# Revit family: DC_Holyoake_OutsideLouver_OHCL-C-124_supply_12
name_source: partatom
category: Air Terminals
revit_build: Autodesk Revit 2013 (Build: 20120221_2030(x64)
units: mm (PartAtom-declared; Revit-internal decimal feet)

## types (2) — shared parameters
Accessories = Aluminium Bird mesh or insect mesh (fibreglass)
Blade Height = 89.8 mm
Blade Offset = 3.05 mm
Blade Pitch = 76.2 mm  [stored 0.25 ft]
Blade Width = 97.1 mm  [stored 0.31857 ft]
Channel Thickness = 103.2 mm  [stored 0.338583 ft]
Channel Width = 25.4 mm  [stored 0.0833333 ft]
Gang Bar Width (plus min. 300mm clearance) = 50 mm  [stored 0.164042 ft]
Gang Bar with Actuator Width (plus min. 300mm clearance) = 150 mm  [stored 0.492126 ft]
Manufacturer = Holyoake
Max Flow = 5000.0 L/s
Min Flow = 100.0 L/s
Overall Depth = 38.3 mm  [stored 0.125656 ft]
Static Pressure Max = 60.0 Pa
Static Pressure Min = 5.0 Pa

## per-type parameters (varying)
| type | Blade Array Count | Blade Count | Blade Cut Setout | Blade Length | Closable Blade Gang Bar | Connector Height | Connector Width | Description | Exact Neck Height | Exact Neck Width | Material - Body | Material - Face | Nominal Height | Nominal Width | Overall Opening | Top Blade Height | Type Comments | URL |
| OHCL-C-124 | 10.094488 | 9 | 685.8 mm | 699.2 mm  [stored 2.29396 ft] | Yes | 745.2 mm | 675.2 mm  [stored 2.21522 ft] | Closable Weather Louvres shall be Holyoake Model OHCL-C-124 straight profile 100mm louvred blades set at 76mm centres and constructed in a channel (C) frame to suit the installation profile. Each Blade shall be fitted with a concealed damper blade pivoted on the underside of each fixed blade which is gang operated by either manual or motorised means. Closable Weather Louvres shall be of extruded aluminium construction and finished in natural anodised or powdercoat and fitted with accessories and dampers where indicated as manufactured by Holyoake. | 820 mm  [stored 2.69029 ft] | 750 mm  [stored 2.46063 ft] | Holyoake Aluminium | Holyoake Aluminium | 826 mm  [stored 2.70997 ft] | 756 mm  [stored 2.48031 ft] | 769.2 mm  [stored 2.52362 ft] | 83.4 mm | 124mm Closable Horizontal Louvers in Channel Surround | http://www.holyoake.com |
| OHL-C-124 | 10.619423 | 10 | 762 mm  [stored 2.5 ft] | 684.2 mm  [stored 2.24475 ft] | No | 785.2 mm  [stored 2.57612 ft] | 660.2 mm  [stored 2.16601 ft] | Holyoake Outside Horizontal Louvre | 860 mm | 735 mm  [stored 2.41142 ft] | <By Category> | <By Category> | 866 mm | 741 mm  [stored 2.4311 ft] | 809.2 mm | 47.2 mm | 124mm Horizontal Louvers in Channel Surround | http://www.productspec.net |

note: column(s) folded — value = type name in every type: Model

note: [stored X ft] marks values corroborated as IEEE doubles in the binary element streams (Revit-internal decimal feet)

## geometry (parser evidence)
native form markers: Blend x6, Sweep x13
no freeform markers — native parametric forms only
